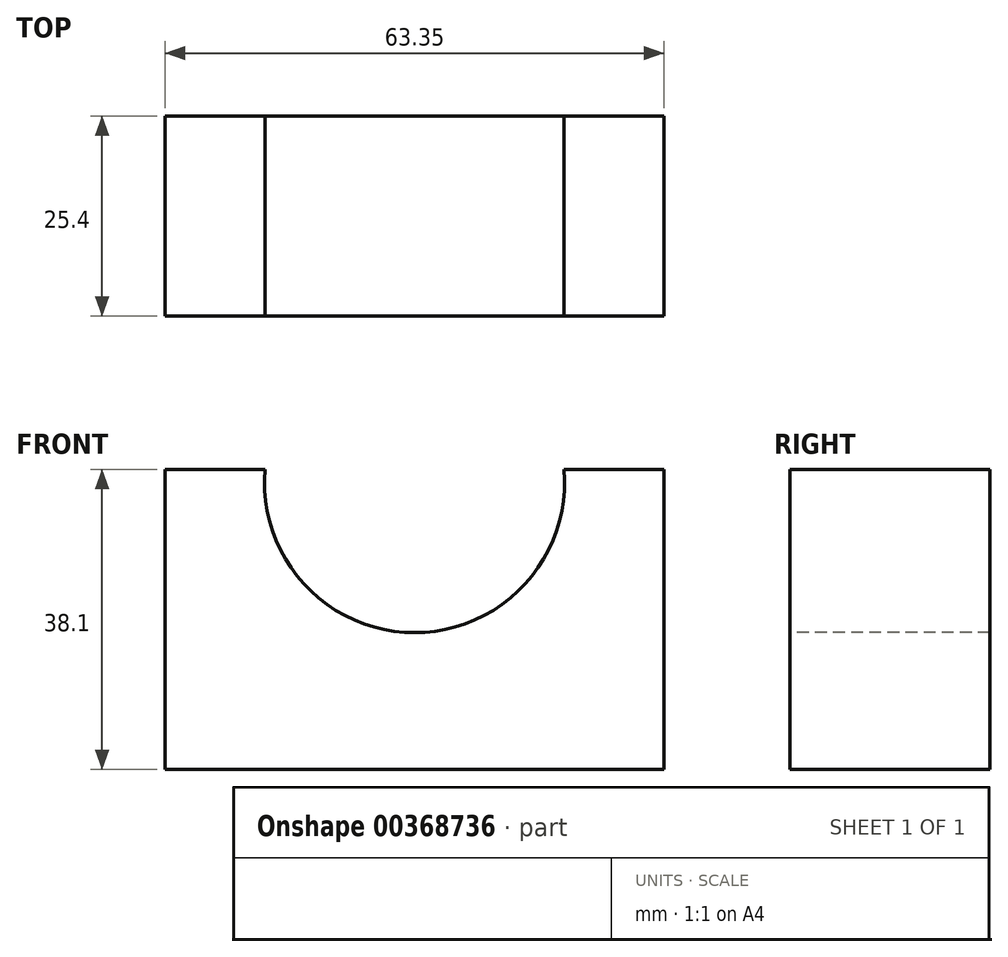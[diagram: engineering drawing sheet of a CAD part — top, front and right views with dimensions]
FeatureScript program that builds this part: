
annotation { "Feature Type Name" : "Feature", "Feature Type Description" : "" }
export const myFeature = defineFeature(function(context is Context, id is Id, definition is map)
    precondition{}
    {
        {
            var Q0;
            Q0=qCreatedBy(makeId("Front.planeOp"),FACE);
            var sketch = newSketch(context, id + "F0", { "sketchPlane" : qUnion([Q0])});
            skLineSegment(sketch, "E0", {"start": v(0, 38.1) * mm, "end": v(0, 0) * mm});
            skLineSegment(sketch, "E1", {"start": v(0, 0) * mm, "end": v(63.35, 0) * mm});
            skLineSegment(sketch, "E2", {"start": v(63.35, 0) * mm, "end": v(63.35, 38.1) * mm});
            skLineSegment(sketch, "E3", {"start": v(63.35, 38.1) * mm, "end": v(50.65, 38.1) * mm});
            skLineSegment(sketch, "E4", {"start": v(0, 38.1) * mm, "end": v(12.7, 38.1) * mm});
            skArc(sketch, "E5", {"start": v(12.7, 38.1) * mm, "mid": v(31.68, 17.38) * mm, "end": v(50.65, 38.1) * mm});
            skSolve(sketch);
        }
        {
            var Q0;
            Q0 = qSketchRegion(id + "F0", true);
            extrude(context, id + "F1", {"entities" : qUnion([Q0]), "oppositeDirection" : true, "depth" : 25.4 * mm});
        }
    });
